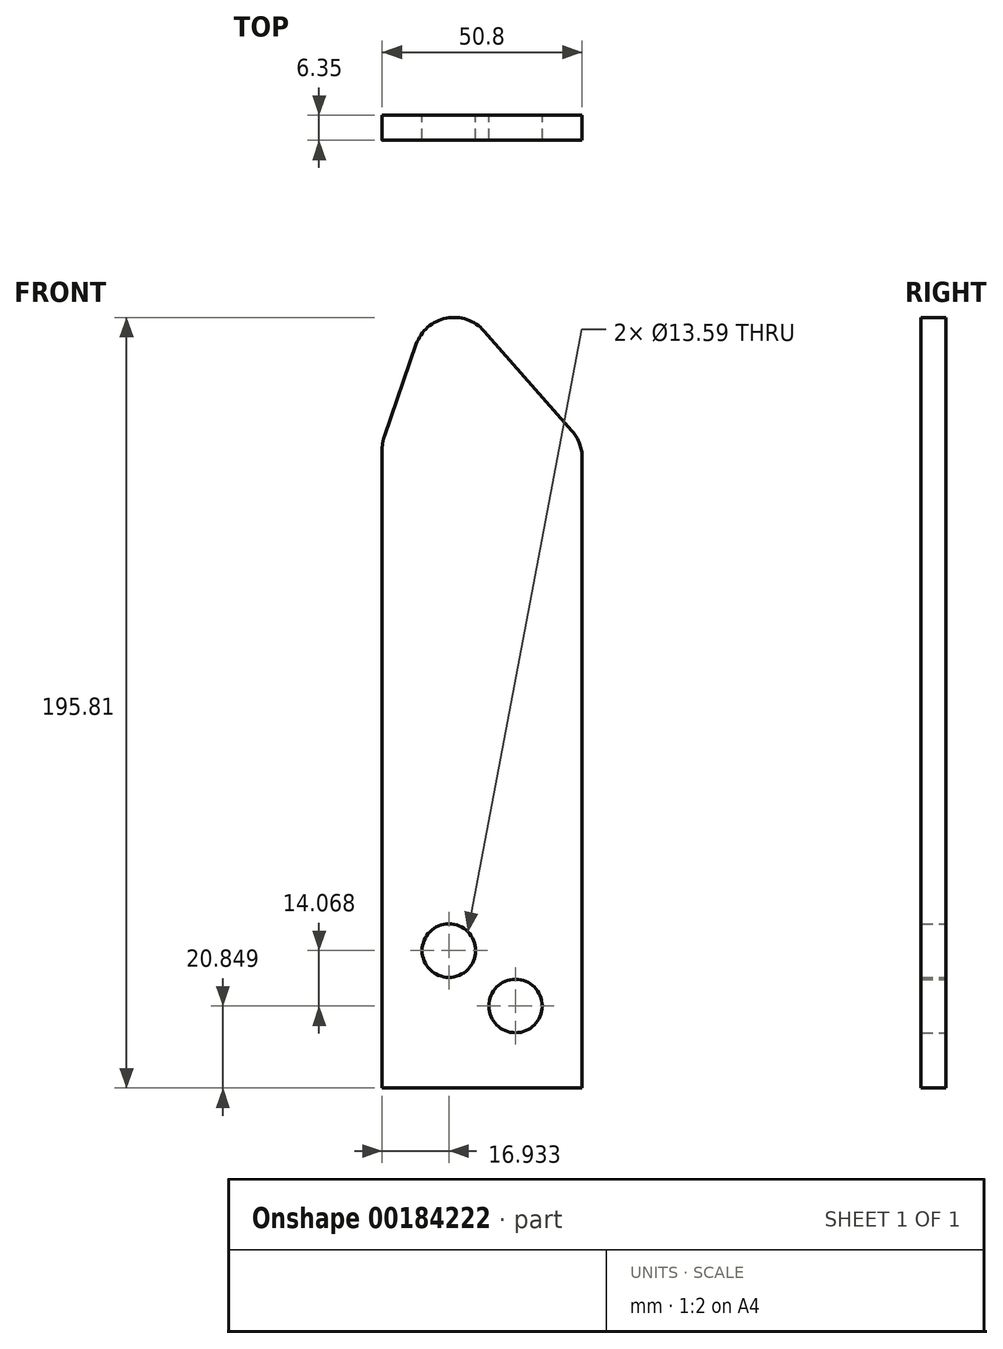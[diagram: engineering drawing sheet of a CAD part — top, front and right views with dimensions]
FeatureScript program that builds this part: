
annotation { "Feature Type Name" : "Feature", "Feature Type Description" : "" }
export const myFeature = defineFeature(function(context is Context, id is Id, definition is map)
    precondition{}
    {
        {
            var Q0;
            Q0=qCreatedBy(makeId("Front.planeOp"),FACE);
            var sketch = newSketch(context, id + "F0", { "sketchPlane" : qUnion([Q0])});
            skLineSegment(sketch, "E0", {"start": v(0, 0) * mm, "end": v(0, 162.3) * mm});
            skLineSegment(sketch, "E1", {"start": v(50.8, 0) * mm, "end": v(50.8, 160.18) * mm});
            skLineSegment(sketch, "E2", {"start": v(0, 0) * mm, "end": v(16.93, 0) * mm});
            skLineSegment(sketch, "E3", {"start": v(16.93, 0) * mm, "end": v(33.87, 0) * mm});
            skLineSegment(sketch, "E4", {"start": v(33.87, 0) * mm, "end": v(50.8, 0) * mm});
            skLineSegment(sketch, "E5", {"start": v(33.87, 0) * mm, "end": v(33.87, 177.8) * mm, "construction": true});
            skLineSegment(sketch, "E6", {"start": v(16.93, 177.8) * mm, "end": v(16.93, 0) * mm, "construction": true});
            skCircle(sketch, "E7", {"center": v(33.87, 20.85) * mm, "radius": 6.8 * mm});
            skCircle(sketch, "E8", {"center": v(16.93, 34.92) * mm, "radius": 6.8 * mm});
            skLineSegment(sketch, "E9", {"start": v(48.27, 166.89) * mm, "end": v(25.88, 192.36) * mm});
            skLineSegment(sketch, "E10", {"start": v(8.64, 188.97) * mm, "end": v(0.56, 165.62) * mm});
            skPoint(sketch, "E11.visualSharp", {"position": v(50.8, 164) * mm});
            skArc(sketch, "E11.filletArc", {"start": v(50.8, 160.18) * mm, "mid": v(50.15, 163.76) * mm, "end": v(48.27, 166.89) * mm});
            skPoint(sketch, "E12.visualSharp", {"position": v(14.35, 205.46) * mm});
            skArc(sketch, "E12.filletArc", {"start": v(25.88, 192.36) * mm, "mid": v(16.29, 195.62) * mm, "end": v(8.64, 188.97) * mm});
            skPoint(sketch, "E13.visualSharp", {"position": v(0, 164) * mm});
            skArc(sketch, "E13.filletArc", {"start": v(0.56, 165.62) * mm, "mid": v(0.14, 163.98) * mm, "end": v(0, 162.3) * mm});
            skSolve(sketch);
        }
        {
            var Q0;
            Q0=makeQuery(id+"F0.imprint","IMPRINT",FACE,{"disambiguationData":[TD([[makeQuery(id+"F0.imprint","IMPRINT",EDGE,{"derivedFrom":sQuery(id+"F0.wireOp",EDGE,"E0")}),-1.0]])]});
            extrude(context, id + "F1", {"entities" : qUnion([Q0]), "depth" : 6.35 * mm});
        }
    });
